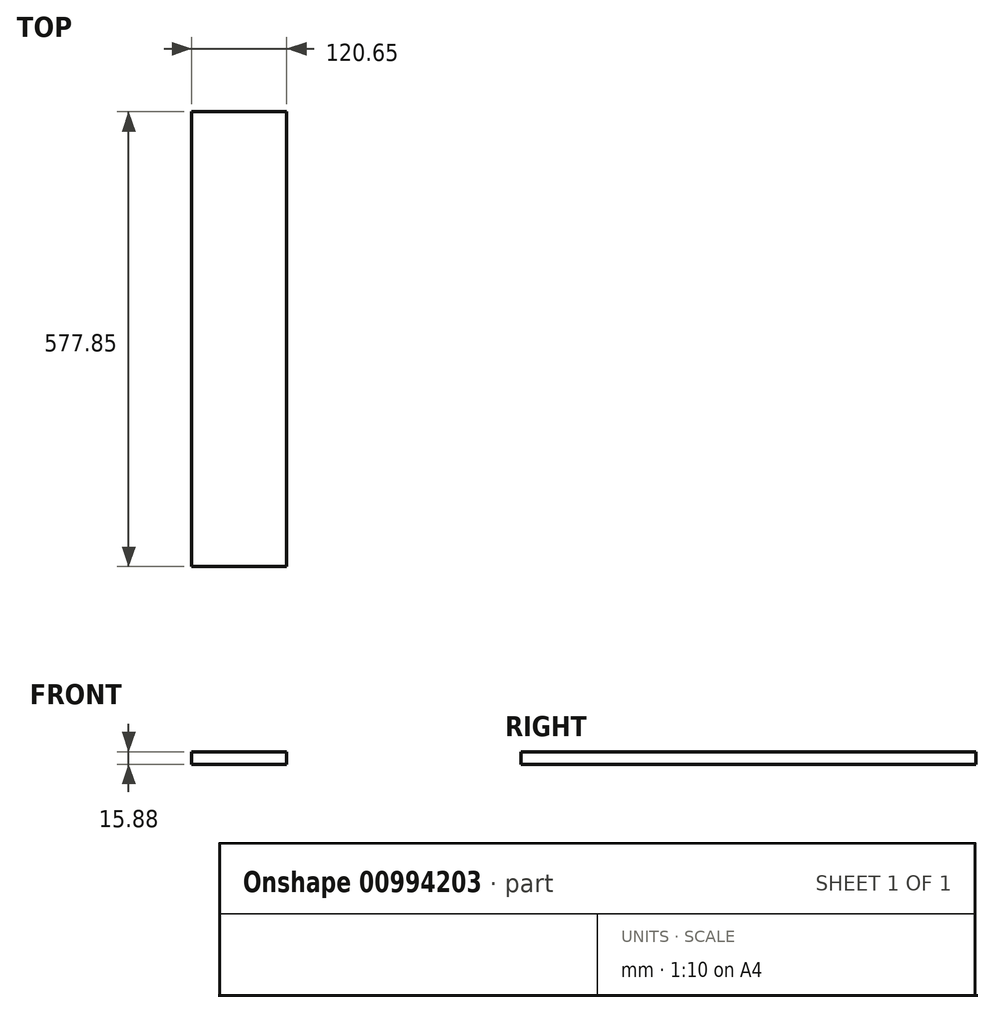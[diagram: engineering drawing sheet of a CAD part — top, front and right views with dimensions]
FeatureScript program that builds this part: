
annotation { "Feature Type Name" : "Feature", "Feature Type Description" : "" }
export const myFeature = defineFeature(function(context is Context, id is Id, definition is map)
    precondition{}
    {
        {
            var Q0;
            Q0=qCreatedBy(makeId("Top.planeOp"),FACE);
            var sketch = newSketch(context, id + "F0", { "sketchPlane" : qUnion([Q0])});
            skLineSegment(sketch, "E0.bottom", {"start": v(0, 0) * mm, "end": v(120.65, 0) * mm});
            skLineSegment(sketch, "E0.top", {"start": v(0, 577.85) * mm, "end": v(120.65, 577.85) * mm});
            skLineSegment(sketch, "E0.left", {"start": v(0, 0) * mm, "end": v(0, 577.85) * mm});
            skLineSegment(sketch, "E0.right", {"start": v(120.65, 0) * mm, "end": v(120.65, 577.85) * mm});
            skSolve(sketch);
        }
        {
            var Q0;
            Q0 = qSketchRegion(id + "F0", true);
            extrude(context, id + "F1", {"entities" : qUnion([Q0]), "depth" : 15.88 * mm, "offsetDistance" : 25.4 * mm});
        }
    });
